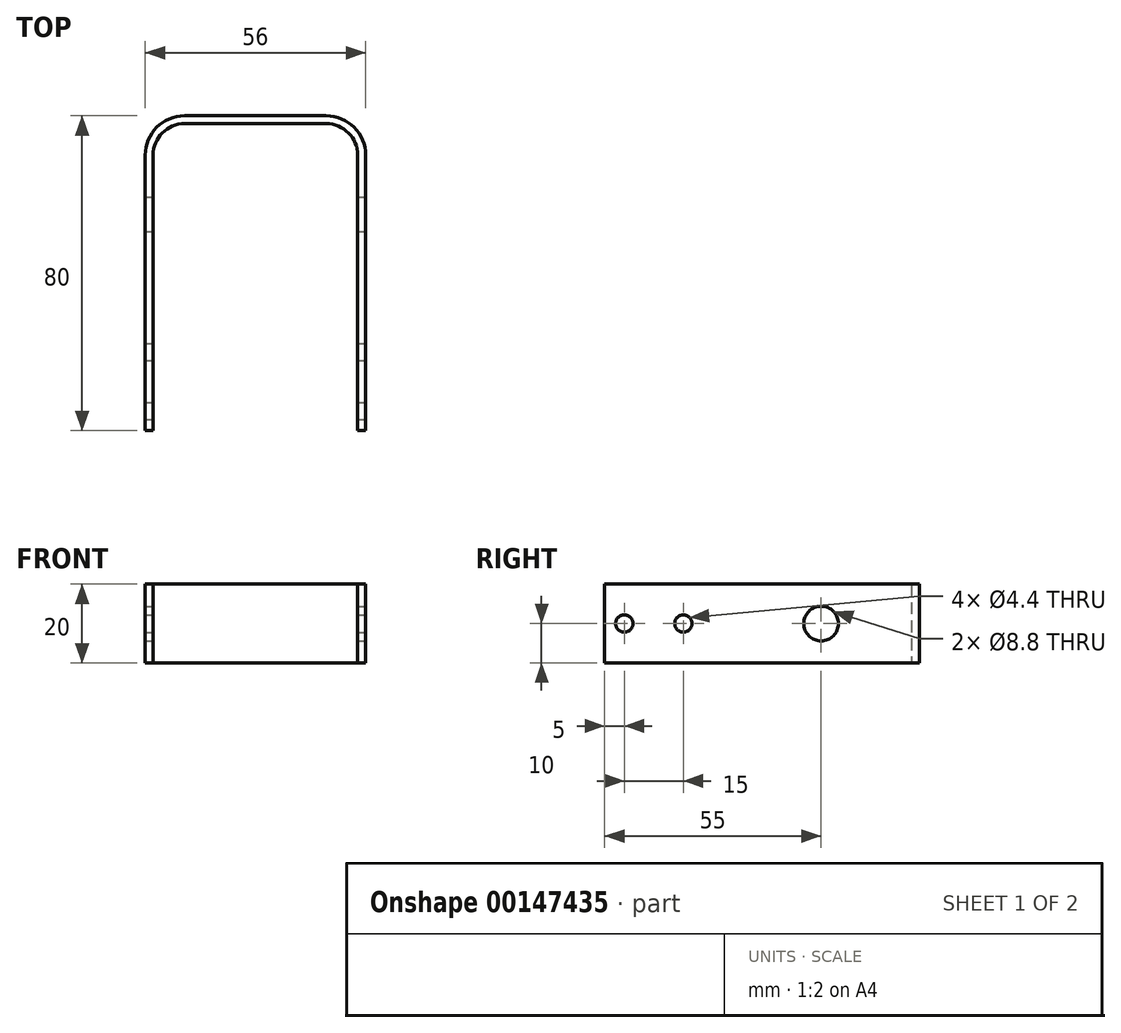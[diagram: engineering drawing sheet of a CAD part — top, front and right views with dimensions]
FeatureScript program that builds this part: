
annotation { "Feature Type Name" : "Feature", "Feature Type Description" : "" }
export const myFeature = defineFeature(function(context is Context, id is Id, definition is map)
    precondition{}
    {
        {
            var Q0;
            Q0=qCreatedBy(makeId("Top.planeOp"),FACE);
            var sketch = newSketch(context, id + "F0", { "sketchPlane" : qUnion([Q0])});
            skLineSegment(sketch, "E0", {"start": v(0, 0) * mm, "end": v(0, 70) * mm});
            skLineSegment(sketch, "E1", {"start": v(10, 80) * mm, "end": v(46, 80) * mm});
            skLineSegment(sketch, "E2", {"start": v(56, 70) * mm, "end": v(56, 0) * mm});
            skPoint(sketch, "E3.visualSharp", {"position": v(0, 80) * mm});
            skArc(sketch, "E3.filletArc", {"start": v(10, 80) * mm, "mid": v(2.93, 77.07) * mm, "end": v(0, 70) * mm});
            skPoint(sketch, "E4.visualSharp", {"position": v(56, 80) * mm});
            skArc(sketch, "E4.filletArc", {"start": v(56, 70) * mm, "mid": v(53.07, 77.07) * mm, "end": v(46, 80) * mm});
            skLineSegment(sketch, "E5.0", {"start": v(54, 70) * mm, "end": v(54, 0) * mm});
            skLineSegment(sketch, "E5.1", {"start": v(2, 0) * mm, "end": v(2, 70) * mm});
            skArc(sketch, "E5.2", {"start": v(10, 78) * mm, "mid": v(4.34, 75.66) * mm, "end": v(2, 70) * mm});
            skLineSegment(sketch, "E5.3", {"start": v(10, 78) * mm, "end": v(46, 78) * mm});
            skArc(sketch, "E5.4", {"start": v(54, 70) * mm, "mid": v(51.66, 75.66) * mm, "end": v(46, 78) * mm});
            skLineSegment(sketch, "E6", {"start": v(2, 0) * mm, "end": v(0, 0) * mm});
            skLineSegment(sketch, "E7", {"start": v(56, 0) * mm, "end": v(54, 0) * mm});
            skSolve(sketch);
        }
        {
            var Q0;
            Q0=makeQuery(id+"F0.imprint","IMPRINT",FACE,{"disambiguationData":[TD([[makeQuery(id+"F0.imprint","IMPRINT",EDGE,{"derivedFrom":sQuery(id+"F0.wireOp",EDGE,"E0")}),-1.0]])]});
            extrude(context, id + "F1", {"entities" : qUnion([Q0]), "depth" : 20 * mm});
        }
        {
            var Q0;
            Q0=makeQuery(id+"F1.opExtrude","SWEPT_FACE",FACE,{"disambiguationData":[OSD([sQuery(id+"F0.wireOp",EDGE,"E2")])]});
            var sketch = newSketch(context, id + "F2", { "sketchPlane" : qUnion([Q0])});
            skPoint(sketch, "E8", {"position": v(55, 10) * mm});
            skPoint(sketch, "E8.positionSnap0", {"position": v(0, 10) * mm});
            skSolve(sketch);
        }
        {
            var Q0;
            Q0=sQuery(id+"F2.wireOp",VERTEX,"E8");
            var Q1;
            Q1=makeQuery(id+"F1.opExtrude","SWEPT_BODY",BODY,{"disambiguationData":[OSD([sQuery(id+"F0.wireOp",EDGE,"E0"),sQuery(id+"F0.wireOp",EDGE,"E1"),sQuery(id+"F0.wireOp",EDGE,"E2"),sQuery(id+"F0.wireOp",EDGE,"E3.filletArc"),sQuery(id+"F0.wireOp",EDGE,"E4.filletArc"),sQuery(id+"F0.wireOp",EDGE,"E5.0"),sQuery(id+"F0.wireOp",EDGE,"E5.1"),sQuery(id+"F0.wireOp",EDGE,"E5.2"),sQuery(id+"F0.wireOp",EDGE,"E5.3"),sQuery(id+"F0.wireOp",EDGE,"E5.4"),sQuery(id+"F0.wireOp",EDGE,"E6"),sQuery(id+"F0.wireOp",EDGE,"E7")])]});
            hole(context, id + "F3", {"style" : HoleStyle.SIMPLE, "endStyle" : HoleEndStyle.THROUGH, "standardTappedOrClearance" : lookupTablePath({ "standard" : "ISO", "fit" : "Normal", "size" : "M8", "type" : "Clearance" }), "standardBlindInLast" : lookupTablePath({ "fit" : "Standard", "standard" : "ISO", "size" : "M8", "type" : "Clearance" }), "holeDiameter" : 8.8 * mm, "locations" : qUnion([Q0]), "scope" : qUnion([Q1]), "isTappedThrough" : true});
        }
        {
            var Q0;
            Q0=makeQuery(id+"F1.opExtrude","SWEPT_FACE",FACE,{"disambiguationData":[OSD([sQuery(id+"F0.wireOp",EDGE,"E2")])]});
            var sketch = newSketch(context, id + "F4", { "sketchPlane" : qUnion([Q0])});
            skPoint(sketch, "E9", {"position": v(5, 10) * mm});
            skPoint(sketch, "E9.positionSnap0", {"position": v(0, 10) * mm});
            skPoint(sketch, "E10", {"position": v(20, 10) * mm});
            skSolve(sketch);
        }
        {
            var Q0;
            Q0=sQuery(id+"F4.wireOp",VERTEX,"E9");
            var Q1;
            Q1=sQuery(id+"F4.wireOp",VERTEX,"E10");
            var Q2;
            Q2=makeQuery(id+"F1.opExtrude","SWEPT_BODY",BODY,{"disambiguationData":[OSD([sQuery(id+"F0.wireOp",EDGE,"E0"),sQuery(id+"F0.wireOp",EDGE,"E1"),sQuery(id+"F0.wireOp",EDGE,"E2"),sQuery(id+"F0.wireOp",EDGE,"E3.filletArc"),sQuery(id+"F0.wireOp",EDGE,"E4.filletArc"),sQuery(id+"F0.wireOp",EDGE,"E5.0"),sQuery(id+"F0.wireOp",EDGE,"E5.1"),sQuery(id+"F0.wireOp",EDGE,"E5.2"),sQuery(id+"F0.wireOp",EDGE,"E5.3"),sQuery(id+"F0.wireOp",EDGE,"E5.4"),sQuery(id+"F0.wireOp",EDGE,"E6"),sQuery(id+"F0.wireOp",EDGE,"E7")])]});
            hole(context, id + "F5", {"style" : HoleStyle.SIMPLE, "endStyle" : HoleEndStyle.THROUGH, "standardTappedOrClearance" : lookupTablePath({ "standard" : "ISO", "fit" : "Normal", "size" : "M4", "type" : "Clearance" }), "standardBlindInLast" : lookupTablePath({ "fit" : "Standard", "standard" : "ISO", "size" : "M4", "type" : "Clearance" }), "holeDiameter" : 4.4 * mm, "locations" : qUnion([Q0, Q1]), "scope" : qUnion([Q2]), "isTappedThrough" : true});
        }
    });
